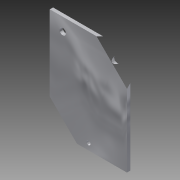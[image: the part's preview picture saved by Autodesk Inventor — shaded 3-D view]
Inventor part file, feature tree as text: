
AUTODESK INVENTOR PART (.ipt)
format: ipt  version: 2015 SP1 (Build 190203100, 203)  size: 115,200 bytes
history: native  units: in
note: dims shown in document units (in); Inventor stores cm internally (conversion verified against a paired STEP export)
features: hole x2, sketch x2, projected_geometry x2, extrude x1
ambient origin geometry x8: Origin, YZ Plane, XZ Plane, XY Plane, X Axis, Y Axis, Z Axis, Center Point
bodies: Solid1 (feature_tree)
feature tree (7):
  extrude  "Extrusion1"  Depth=0.125in
  hole  "Hole1"  [1 undecoded]
  hole  "Hole2"  [1 undecoded]
  sketch  "Sketch1"  dims[d0=2.0in d1=0.125in]
  projected_geometry  "Projected Loop1"
  sketch  "Sketch3"  dims[d2=1.0in d3=0.0in d4=0.125in d5=3.0in d6=0.0in d11=0.25in d12=0.75in d13=0.375in d14=0.25in d15=0.5635in d16=1.0in d17=0.8108in d18=0.25in d19=1.5in d20=0.1562in d21=0.75in d22=0.375in d23=0.25in d24=0.5635in d25=1.0in d26=0.8108in]
  projected_geometry  "Projected Loop2"
note: 2 required parameter values undecoded (feature->parameter linkage not recoverable at this tier; creation-order binding heuristic only, values carry confidence <= 0.55)
